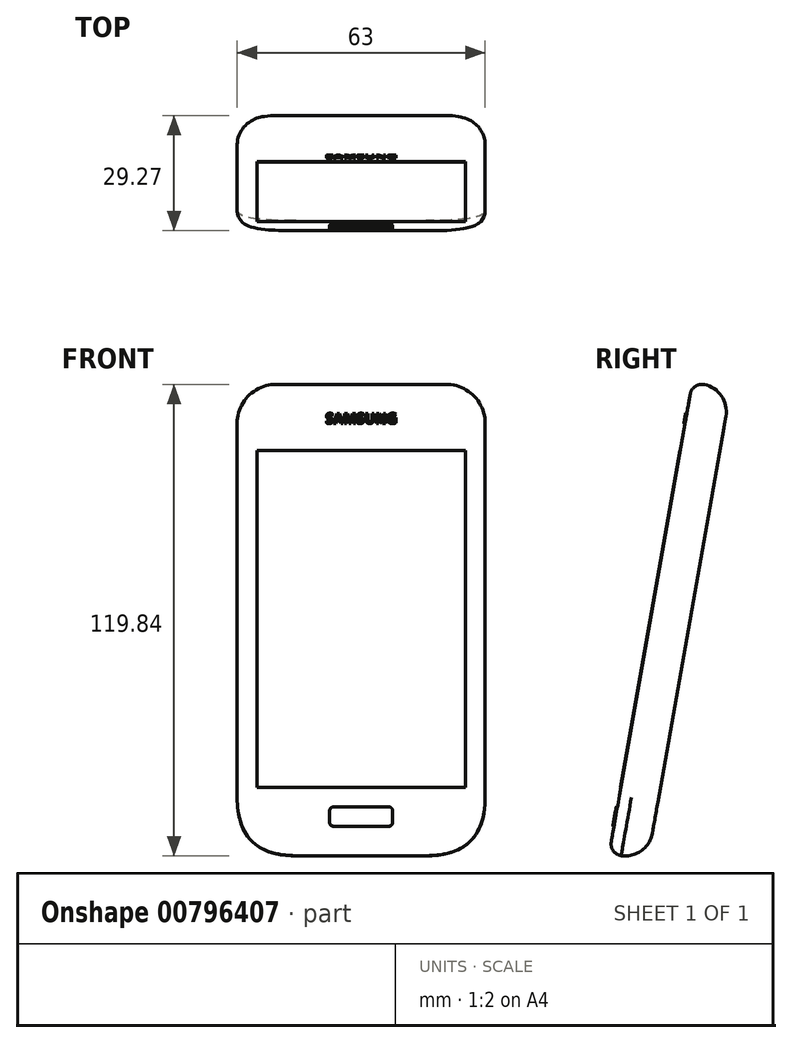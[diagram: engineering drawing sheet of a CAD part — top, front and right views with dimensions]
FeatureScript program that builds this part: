
annotation { "Feature Type Name" : "Feature", "Feature Type Description" : "" }
export const myFeature = defineFeature(function(context is Context, id is Id, definition is map)
    precondition{}
    {
        {
            var Q0;
            Q0=qCreatedBy(makeId("Top.planeOp"),FACE);
            var sketch = newSketch(context, id + "F0", { "sketchPlane" : qUnion([Q0])});
            skLineSegment(sketch, "E0.bottom", {"start": v(-31.5, 4.95) * mm, "end": v(31.5, 4.95) * mm});
            skLineSegment(sketch, "E0.top", {"start": v(-31.5, -4.95) * mm, "end": v(31.5, -4.95) * mm});
            skLineSegment(sketch, "E0.left", {"start": v(-31.5, 4.95) * mm, "end": v(-31.5, -4.95) * mm});
            skLineSegment(sketch, "E0.right", {"start": v(31.5, 4.95) * mm, "end": v(31.5, -4.95) * mm});
            skSolve(sketch);
        }
        {
            var Q0;
            Q0=qSketchRegion(id+"F0",true);
            extrude(context, id + "F1", {"entities" : qUnion([Q0]), "depth" : 121.55 * mm, "offsetDistance" : 25 * mm});
        }
        {
            var Q0;
            Q0=makeQuery(id+"F1.opExtrude","CAP_EDGE",EDGE,{"disambiguationData":[OSD([sQuery(id+"F0.wireOp",EDGE,"E0.right")])],"isStart":true});
            var Q1;
            Q1=makeQuery(id+"F1.opExtrude","CAP_EDGE",EDGE,{"disambiguationData":[OSD([sQuery(id+"F0.wireOp",EDGE,"E0.left")])],"isStart":true});
            fillet(context, id + "F2", {"entities" : qUnion([Q0, Q1]), "radius" : 15 * mm, "tangentPropagation" : true, "rho" : 0.5, "crossSection" : FilletCrossSection.CONIC, "allowEdgeOverflow" : false});
        }
        {
            var Q0;
            Q0=makeQuery(id+"F1.opExtrude","CAP_EDGE",EDGE,{"disambiguationData":[OSD([sQuery(id+"F0.wireOp",EDGE,"E0.right")])],"isStart":false});
            var Q1;
            Q1=makeQuery(id+"F1.opExtrude","CAP_EDGE",EDGE,{"disambiguationData":[OSD([sQuery(id+"F0.wireOp",EDGE,"E0.left")])],"isStart":false});
            fillet(context, id + "F3", {"entities" : qUnion([Q0, Q1]), "radius" : 10 * mm, "tangentPropagation" : true, "allowEdgeOverflow" : false});
        }
        {
            var Q0;
            Q0=makeQuery(id+"F1.opExtrude","SWEPT_FACE",FACE,{"disambiguationData":[OSD([sQuery(id+"F0.wireOp",EDGE,"E0.top")])]});
            var sketch = newSketch(context, id + "F4", { "sketchPlane" : qUnion([Q0])});
            skLineSegment(sketch, "E1.bottom", {"start": v(-7, 12) * mm, "end": v(7, 12) * mm});
            skLineSegment(sketch, "E1.top", {"start": v(-7, 7) * mm, "end": v(7, 7) * mm});
            skLineSegment(sketch, "E1.left", {"start": v(-8, 11) * mm, "end": v(-8, 8) * mm});
            skLineSegment(sketch, "E1.right", {"start": v(8, 11) * mm, "end": v(8, 8) * mm});
            skPoint(sketch, "E2.visualSharp", {"position": v(-8, 12) * mm});
            skArc(sketch, "E2.filletArc", {"start": v(-7, 12) * mm, "mid": v(-7.7, 11.7) * mm, "end": v(-8, 11) * mm});
            skPoint(sketch, "E3.visualSharp", {"position": v(-8, 7) * mm});
            skArc(sketch, "E3.filletArc", {"start": v(-8, 8) * mm, "mid": v(-7.7, 7.3) * mm, "end": v(-7, 7) * mm});
            skPoint(sketch, "E4.visualSharp", {"position": v(8, 7) * mm});
            skArc(sketch, "E4.filletArc", {"start": v(7, 7) * mm, "mid": v(7.7, 7.3) * mm, "end": v(8, 8) * mm});
            skPoint(sketch, "E5.visualSharp", {"position": v(8, 12) * mm});
            skArc(sketch, "E5.filletArc", {"start": v(8, 11) * mm, "mid": v(7.7, 11.7) * mm, "end": v(7, 12) * mm});
            skSolve(sketch);
        }
        {
            var Q0;
            Q0=qSketchRegion(id+"F4",true);
            extrude(context, id + "F5", {"entities" : qUnion([Q0]), "operationType" : NewBodyOperationType.ADD, "depth" : 0.3 * mm, "offsetDistance" : 25 * mm});
        }
        {
            var Q0;
            Q0=makeQuery(id+"F2.opFillet","BLEND_EDGE",EDGE,{"blendedFrom":[makeQuery(id+"F1.opExtrude","CAP_EDGE",EDGE,{"disambiguationData":[OSD([sQuery(id+"F0.wireOp",EDGE,"E0.right")])],"isStart":true}),makeQuery(id+"F1.opExtrude","SWEPT_FACE",FACE,{"disambiguationData":[OSD([sQuery(id+"F0.wireOp",EDGE,"E0.bottom")])]})],"blendedInto":[makeQuery(id+"F1.opExtrude","SWEPT_FACE",FACE,{"disambiguationData":[OSD([sQuery(id+"F0.wireOp",EDGE,"E0.bottom")])]})]});
            fillet(context, id + "F6", {"entities" : qUnion([Q0]), "radius" : 7 * mm, "tangentPropagation" : true, "allowEdgeOverflow" : false});
        }
        {
            var Q0;
            Q0=makeQuery(id+"F2.opFillet","BLEND_EDGE",EDGE,{"blendedFrom":[makeQuery(id+"F1.opExtrude","CAP_EDGE",EDGE,{"disambiguationData":[OSD([sQuery(id+"F0.wireOp",EDGE,"E0.right")])],"isStart":true}),makeQuery(id+"F1.opExtrude","SWEPT_FACE",FACE,{"disambiguationData":[OSD([sQuery(id+"F0.wireOp",EDGE,"E0.top")])]})],"blendedInto":[makeQuery(id+"F1.opExtrude","SWEPT_FACE",FACE,{"disambiguationData":[OSD([sQuery(id+"F0.wireOp",EDGE,"E0.top")])]})]});
            fillet(context, id + "F7", {"entities" : qUnion([Q0]), "radius" : 3 * mm, "tangentPropagation" : true, "allowEdgeOverflow" : false});
        }
        {
            var Q0;
            Q0=makeQuery(id+"F1.opExtrude","SWEPT_FACE",FACE,{"disambiguationData":[OSD([sQuery(id+"F0.wireOp",EDGE,"E0.top")])]});
            var sketch = newSketch(context, id + "F8", { "sketchPlane" : qUnion([Q0])});
            skText(sketch, "E6", { "text": "SAMSUNG", "fontName": "OpenSans-Bold.ttf"});
            const initialGuessF8  = {"E6": [-0.009, 0.11096, 1, 0, 0.00259]};
            skSetInitialGuess(sketch, initialGuessF8);
            skSolve(sketch);
        }
        {
            var Q0;
            Q0=qSketchRegion(id+"F8",true);
            extrude(context, id + "F9", {"entities" : qUnion([Q0]), "operationType" : NewBodyOperationType.ADD, "depth" : 0.3 * mm, "offsetDistance" : 25 * mm});
        }
        {
            var Q0;
            Q0=makeQuery(id+"F1.opExtrude","SWEPT_BODY",BODY,{"disambiguationData":[OSD([sQuery(id+"F0.wireOp",EDGE,"E0.bottom"),sQuery(id+"F0.wireOp",EDGE,"E0.top"),sQuery(id+"F0.wireOp",EDGE,"E0.left"),sQuery(id+"F0.wireOp",EDGE,"E0.right")])]});
            transform(context, id + "F10", {"entities" : qUnion([Q0]), "transformType" : TransformType.TRANSLATION_3D, "dx" : 37.5 * mm, "dy" : 0 * mm, "dz" : 30 * mm, "makeCopy" : false});
        }
        {
            var Q0;
            Q0=qCreatedBy(makeId("Front.planeOp"),FACE);
            var sketch = newSketch(context, id + "F11", { "sketchPlane" : qUnion([Q0])});
            skLineSegment(sketch, "E7", {"start": v(-100, 30) * mm, "end": v(100, 30) * mm});
            skSolve(sketch);
        }
        {
            var Q0;
            Q0=makeQuery(id+"F1.opExtrude","SWEPT_BODY",BODY,{"disambiguationData":[OSD([sQuery(id+"F0.wireOp",EDGE,"E0.bottom"),sQuery(id+"F0.wireOp",EDGE,"E0.top"),sQuery(id+"F0.wireOp",EDGE,"E0.left"),sQuery(id+"F0.wireOp",EDGE,"E0.right")])]});
            var Q1;
            Q1=sQuery(id+"F11.wireOp",EDGE,"E7");
            var Q2;
            Q2=sQuery(id+"F11.wireOp",EDGE,"E7");
            transform(context, id + "F12", {"entities" : qUnion([Q0]), "transformType" : TransformType.ROTATION, "transformAxis" : qUnion([Q2]), "angle" : 10 * degree, "oppositeDirection" : true, "makeCopy" : false});
        }
        {
            var Q0;
            {var subQ1=sQuery(id+"F0.wireOp",EDGE,"E0.top");var subQ3=makeQuery(id+"F1.opExtrude","SWEPT_FACE",FACE,{"disambiguationData":[OSD([subQ1])]});var subQ4=subQ3;Q0=makeQuery(id+"F9.boolean.opBoolean","SPLIT",FACE,{"disambiguationData":[TD([makeQuery(id+"F5.opExtrude","SWEPT_FACE",FACE,{"disambiguationData":[OSD([sQuery(id+"F4.wireOp",EDGE,"E1.bottom")])]})])],"derivedFrom":subQ4});}
            var sketch = newSketch(context, id + "F13", { "sketchPlane" : qUnion([Q0])});
            skLineSegment(sketch, "E8.bottom", {"start": v(11, 133.55) * mm, "end": v(64, 133.55) * mm});
            skLineSegment(sketch, "E8.top", {"start": v(11, 46.55) * mm, "end": v(64, 46.55) * mm});
            skLineSegment(sketch, "E8.left", {"start": v(11, 133.55) * mm, "end": v(11, 46.55) * mm});
            skLineSegment(sketch, "E8.right", {"start": v(64, 133.55) * mm, "end": v(64, 46.55) * mm});
            skLineSegment(sketch, "E9", {"start": v(37.5, 148.1) * mm, "end": v(37.5, 32.55) * mm, "construction": true});
            skSolve(sketch);
        }
        {
            var Q0;
            Q0=qSketchRegion(id+"F13",true);
            extrude(context, id + "F14", {"entities" : qUnion([Q0]), "depth" : 0.1 * mm, "offsetDistance" : 25 * mm});
        }
    });
